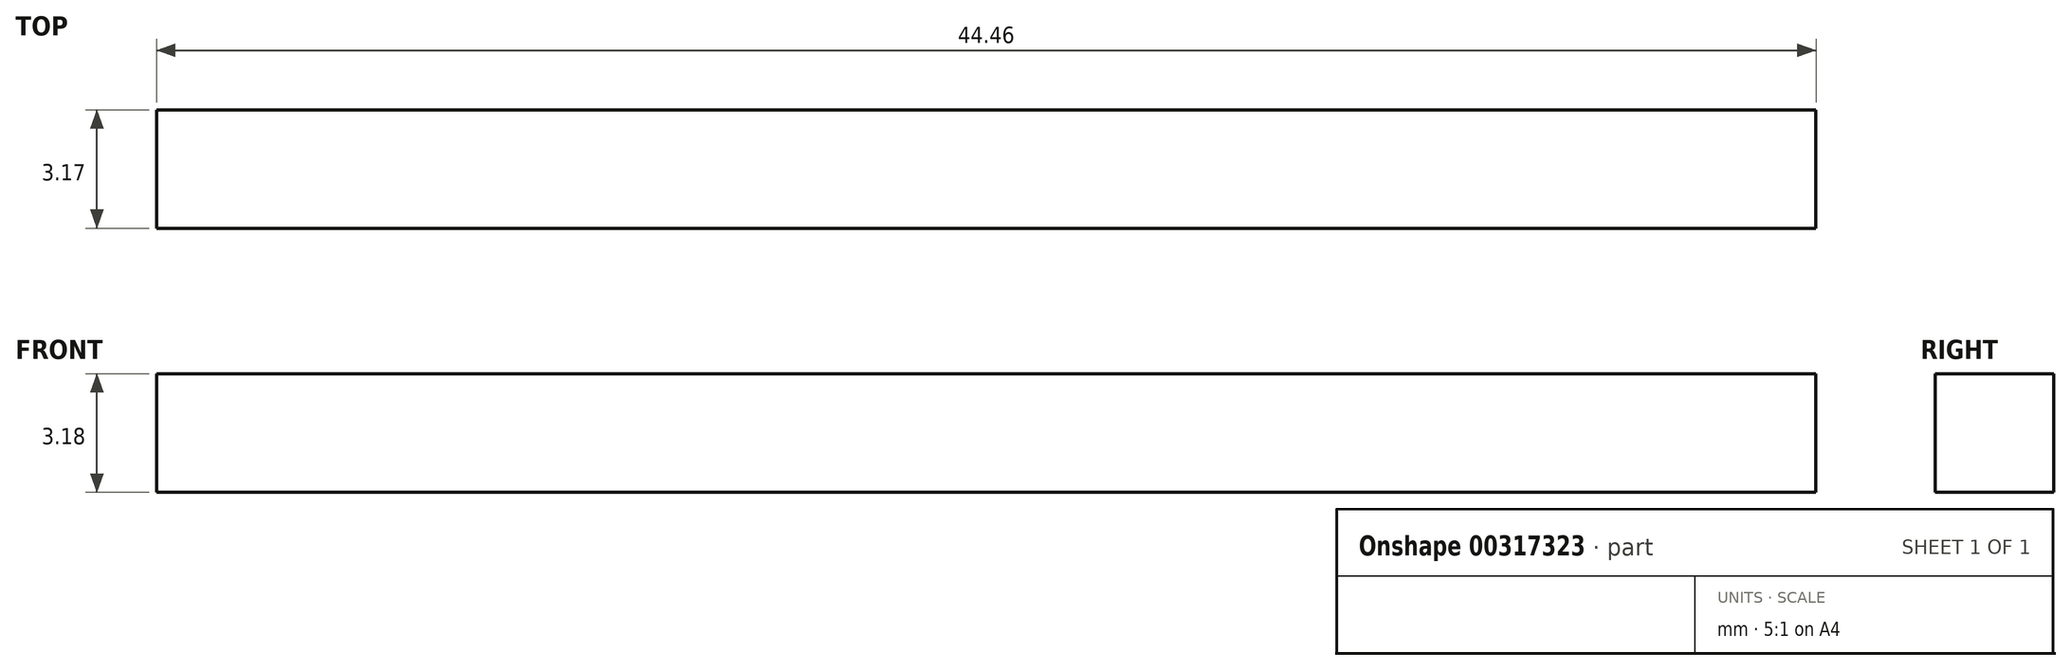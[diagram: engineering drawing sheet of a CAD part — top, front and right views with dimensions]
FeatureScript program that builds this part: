
annotation { "Feature Type Name" : "Feature", "Feature Type Description" : "" }
export const myFeature = defineFeature(function(context is Context, id is Id, definition is map)
    precondition{}
    {
        {
            var Q0;
            Q0=qCreatedBy(makeId("Front.planeOp"),FACE);
            var sketch = newSketch(context, id + "F0", { "sketchPlane" : qUnion([Q0])});
            skLineSegment(sketch, "E0.bottom", {"start": v(22.22, 1.59) * mm, "end": v(-22.23, 1.59) * mm});
            skLineSegment(sketch, "E0.top", {"start": v(22.23, -1.59) * mm, "end": v(-22.22, -1.59) * mm});
            skLineSegment(sketch, "E0.left", {"start": v(22.22, 1.59) * mm, "end": v(22.22, -1.59) * mm});
            skLineSegment(sketch, "E0.right", {"start": v(-22.23, 1.59) * mm, "end": v(-22.22, -1.59) * mm});
            skPoint(sketch, "E0.middle", {"position": v(0, 0) * mm});
            skSolve(sketch);
        }
        {
            var Q0;
            Q0 = qSketchRegion(id + "F0", true);
            extrude(context, id + "F1", {"entities" : qUnion([Q0]), "depth" : 3.17 * mm});
        }
    });
